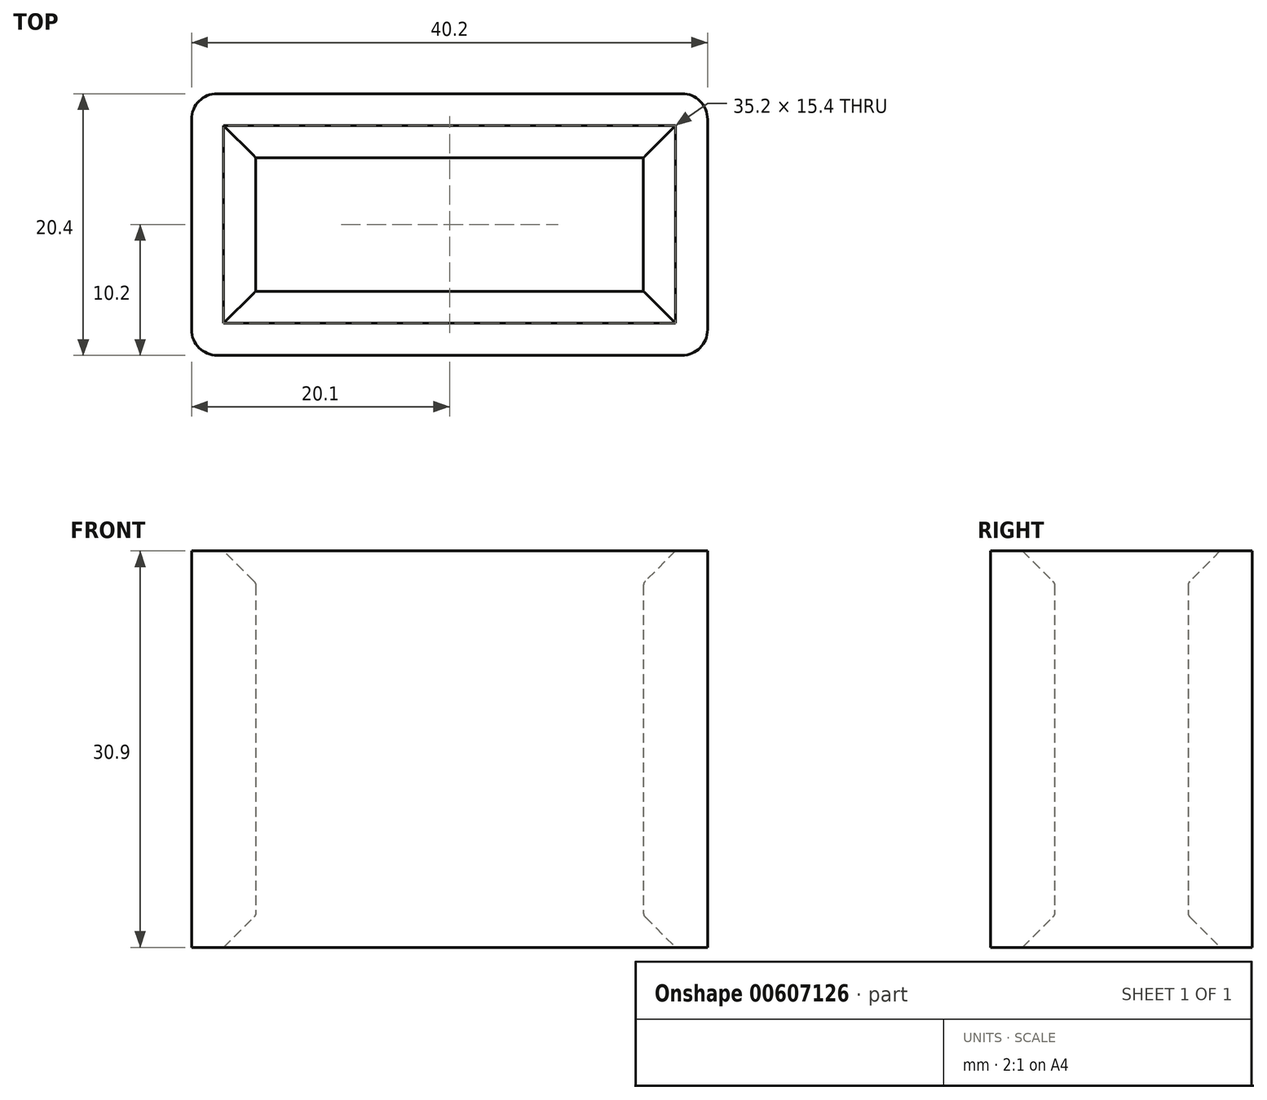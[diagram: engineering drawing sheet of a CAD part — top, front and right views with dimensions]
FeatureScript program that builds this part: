
annotation { "Feature Type Name" : "Feature", "Feature Type Description" : "" }
export const myFeature = defineFeature(function(context is Context, id is Id, definition is map)
    precondition{}
    {
        {
            var Q0;
            Q0=qCreatedBy(makeId("Top.planeOp"),FACE);
            var sketch = newSketch(context, id + "F0", { "sketchPlane" : qUnion([Q0])});
            skLineSegment(sketch, "E0.bottom", {"start": v(20.1, -10.2) * mm, "end": v(-20.1, -10.2) * mm});
            skLineSegment(sketch, "E0.top", {"start": v(20.1, 10.2) * mm, "end": v(-20.1, 10.2) * mm});
            skLineSegment(sketch, "E0.left", {"start": v(20.1, -10.2) * mm, "end": v(20.1, 10.2) * mm});
            skLineSegment(sketch, "E0.right", {"start": v(-20.1, -10.2) * mm, "end": v(-20.1, 10.2) * mm});
            skPoint(sketch, "E0.middle", {"position": v(0, 0) * mm});
            skLineSegment(sketch, "E1.bottom", {"start": v(15.1, -5.2) * mm, "end": v(-15.1, -5.2) * mm});
            skLineSegment(sketch, "E1.top", {"start": v(15.1, 5.2) * mm, "end": v(-15.1, 5.2) * mm});
            skLineSegment(sketch, "E1.left", {"start": v(15.1, -5.2) * mm, "end": v(15.1, 5.2) * mm});
            skLineSegment(sketch, "E1.right", {"start": v(-15.1, -5.2) * mm, "end": v(-15.1, 5.2) * mm});
            skSolve(sketch);
        }
        {
            var Q0;
            Q0=makeQuery(id+"F0.imprint","IMPRINT",FACE,{"disambiguationData":[TD([[makeQuery(id+"F0.imprint","IMPRINT",EDGE,{"derivedFrom":sQuery(id+"F0.wireOp",EDGE,"E0.bottom")}),-1.0]])]});
            extrude(context, id + "F1", {"entities" : qUnion([Q0]), "depth" : 30.9 * mm, "offsetDistance" : 25 * mm});
        }
        {
            var Q0;
            Q0=makeQuery(id+"F1.opExtrude","CAP_EDGE",EDGE,{"disambiguationData":[OSD([sQuery(id+"F0.wireOp",EDGE,"E1.right")])],"isStart":true});
            var Q1;
            Q1=makeQuery(id+"F1.opExtrude","CAP_EDGE",EDGE,{"disambiguationData":[OSD([sQuery(id+"F0.wireOp",EDGE,"E1.bottom")])],"isStart":true});
            var Q2;
            Q2=makeQuery(id+"F1.opExtrude","CAP_EDGE",EDGE,{"disambiguationData":[OSD([sQuery(id+"F0.wireOp",EDGE,"E1.left")])],"isStart":true});
            var Q3;
            Q3=makeQuery(id+"F1.opExtrude","CAP_EDGE",EDGE,{"disambiguationData":[OSD([sQuery(id+"F0.wireOp",EDGE,"E1.top")])],"isStart":true});
            var Q4;
            Q4=makeQuery(id+"F1.opExtrude","CAP_EDGE",EDGE,{"disambiguationData":[OSD([sQuery(id+"F0.wireOp",EDGE,"E1.right")])],"isStart":false});
            var Q5;
            Q5=makeQuery(id+"F1.opExtrude","CAP_EDGE",EDGE,{"disambiguationData":[OSD([sQuery(id+"F0.wireOp",EDGE,"E1.top")])],"isStart":false});
            var Q6;
            Q6=makeQuery(id+"F1.opExtrude","CAP_EDGE",EDGE,{"disambiguationData":[OSD([sQuery(id+"F0.wireOp",EDGE,"E1.left")])],"isStart":false});
            var Q7;
            Q7=makeQuery(id+"F1.opExtrude","CAP_EDGE",EDGE,{"disambiguationData":[OSD([sQuery(id+"F0.wireOp",EDGE,"E1.bottom")])],"isStart":false});
            chamfer(context, id + "F2", {"entities" : qUnion([Q0, Q1, Q2, Q3, Q4, Q5, Q6, Q7]), "width" : 2.5 * mm, "tangentPropagation" : true});
        }
        {
            var Q0;
            Q0=makeQuery(id+"F1.opExtrude","SWEPT_EDGE",EDGE,{"disambiguationData":[OSD([sQuery(id+"F0.wireOp",EDGE,"E0.bottom"),sQuery(id+"F0.wireOp",EDGE,"E0.right")])]});
            var Q1;
            Q1=makeQuery(id+"F1.opExtrude","SWEPT_EDGE",EDGE,{"disambiguationData":[OSD([sQuery(id+"F0.wireOp",EDGE,"E0.top"),sQuery(id+"F0.wireOp",EDGE,"E0.right")])]});
            var Q2;
            Q2=makeQuery(id+"F1.opExtrude","SWEPT_EDGE",EDGE,{"disambiguationData":[OSD([sQuery(id+"F0.wireOp",EDGE,"E0.bottom"),sQuery(id+"F0.wireOp",EDGE,"E0.left")])]});
            var Q3;
            Q3=makeQuery(id+"F1.opExtrude","SWEPT_EDGE",EDGE,{"disambiguationData":[OSD([sQuery(id+"F0.wireOp",EDGE,"E0.top"),sQuery(id+"F0.wireOp",EDGE,"E0.left")])]});
            fillet(context, id + "F3", {"entities" : qUnion([Q0, Q1, Q2, Q3]), "radius" : 2 * mm, "tangentPropagation" : true, "allowEdgeOverflow" : false});
        }
        {
            var Q0;
            {var subQ0=sQuery(id+"F0.wireOp",EDGE,"E1.right");Q0=makeQuery(id+"F2.opChamfer","BLEND_EDGE",EDGE,{"blendedFrom":[makeQuery(id+"F1.opExtrude","CAP_EDGE",EDGE,{"disambiguationData":[OSD([subQ0])],"isStart":false}),makeQuery(id+"F1.opExtrude","SWEPT_FACE",FACE,{"disambiguationData":[OSD([subQ0])]})],"blendedInto":[makeQuery(id+"F1.opExtrude","SWEPT_FACE",FACE,{"disambiguationData":[OSD([subQ0])]})]});}
            var Q1;
            {var subQ0=sQuery(id+"F0.wireOp",EDGE,"E1.top");Q1=makeQuery(id+"F2.opChamfer","BLEND_EDGE",EDGE,{"blendedFrom":[makeQuery(id+"F1.opExtrude","CAP_EDGE",EDGE,{"disambiguationData":[OSD([subQ0])],"isStart":false}),makeQuery(id+"F1.opExtrude","SWEPT_FACE",FACE,{"disambiguationData":[OSD([subQ0])]})],"blendedInto":[makeQuery(id+"F1.opExtrude","SWEPT_FACE",FACE,{"disambiguationData":[OSD([subQ0])]})]});}
            var Q2;
            {var subQ0=sQuery(id+"F0.wireOp",EDGE,"E1.left");Q2=makeQuery(id+"F2.opChamfer","BLEND_EDGE",EDGE,{"blendedFrom":[makeQuery(id+"F1.opExtrude","CAP_EDGE",EDGE,{"disambiguationData":[OSD([subQ0])],"isStart":false}),makeQuery(id+"F1.opExtrude","SWEPT_FACE",FACE,{"disambiguationData":[OSD([subQ0])]})],"blendedInto":[makeQuery(id+"F1.opExtrude","SWEPT_FACE",FACE,{"disambiguationData":[OSD([subQ0])]})]});}
            var Q3;
            {var subQ0=sQuery(id+"F0.wireOp",EDGE,"E1.bottom");Q3=makeQuery(id+"F2.opChamfer","BLEND_EDGE",EDGE,{"blendedFrom":[makeQuery(id+"F1.opExtrude","CAP_EDGE",EDGE,{"disambiguationData":[OSD([subQ0])],"isStart":false}),makeQuery(id+"F1.opExtrude","SWEPT_FACE",FACE,{"disambiguationData":[OSD([subQ0])]})],"blendedInto":[makeQuery(id+"F1.opExtrude","SWEPT_FACE",FACE,{"disambiguationData":[OSD([subQ0])]})]});}
            var Q4;
            {var subQ0=sQuery(id+"F0.wireOp",EDGE,"E1.top");Q4=makeQuery(id+"F2.opChamfer","BLEND_EDGE",EDGE,{"blendedFrom":[makeQuery(id+"F1.opExtrude","CAP_EDGE",EDGE,{"disambiguationData":[OSD([subQ0])],"isStart":true}),makeQuery(id+"F1.opExtrude","SWEPT_FACE",FACE,{"disambiguationData":[OSD([subQ0])]})],"blendedInto":[makeQuery(id+"F1.opExtrude","SWEPT_FACE",FACE,{"disambiguationData":[OSD([subQ0])]})]});}
            var Q5;
            {var subQ0=sQuery(id+"F0.wireOp",EDGE,"E1.right");Q5=makeQuery(id+"F2.opChamfer","BLEND_EDGE",EDGE,{"blendedFrom":[makeQuery(id+"F1.opExtrude","CAP_EDGE",EDGE,{"disambiguationData":[OSD([subQ0])],"isStart":true}),makeQuery(id+"F1.opExtrude","SWEPT_FACE",FACE,{"disambiguationData":[OSD([subQ0])]})],"blendedInto":[makeQuery(id+"F1.opExtrude","SWEPT_FACE",FACE,{"disambiguationData":[OSD([subQ0])]})]});}
            var Q6;
            {var subQ0=sQuery(id+"F0.wireOp",EDGE,"E1.left");Q6=makeQuery(id+"F2.opChamfer","BLEND_EDGE",EDGE,{"blendedFrom":[makeQuery(id+"F1.opExtrude","CAP_EDGE",EDGE,{"disambiguationData":[OSD([subQ0])],"isStart":true}),makeQuery(id+"F1.opExtrude","SWEPT_FACE",FACE,{"disambiguationData":[OSD([subQ0])]})],"blendedInto":[makeQuery(id+"F1.opExtrude","SWEPT_FACE",FACE,{"disambiguationData":[OSD([subQ0])]})]});}
            var Q7;
            {var subQ0=sQuery(id+"F0.wireOp",EDGE,"E1.bottom");Q7=makeQuery(id+"F2.opChamfer","BLEND_EDGE",EDGE,{"blendedFrom":[makeQuery(id+"F1.opExtrude","CAP_EDGE",EDGE,{"disambiguationData":[OSD([subQ0])],"isStart":true}),makeQuery(id+"F1.opExtrude","SWEPT_FACE",FACE,{"disambiguationData":[OSD([subQ0])]})],"blendedInto":[makeQuery(id+"F1.opExtrude","SWEPT_FACE",FACE,{"disambiguationData":[OSD([subQ0])]})]});}
            fillet(context, id + "F4", {"entities" : qUnion([Q0, Q1, Q2, Q3, Q4, Q5, Q6, Q7]), "radius" : .5 * mm, "tangentPropagation" : true, "allowEdgeOverflow" : false});
        }
    });
